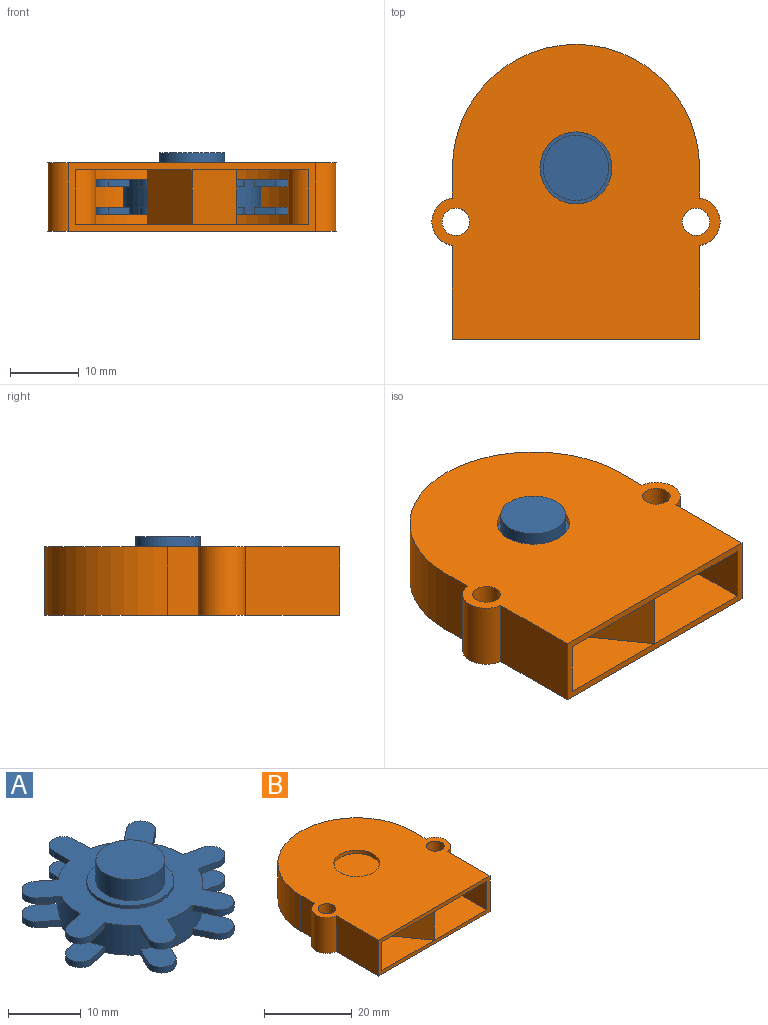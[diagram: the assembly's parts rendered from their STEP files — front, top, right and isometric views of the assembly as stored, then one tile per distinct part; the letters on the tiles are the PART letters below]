
ASSEMBLY  parts=2 mates=1
PART A: 77 faces, bbox 29.3x28.7x11.5 mm
  f0: cylinder r=10mm len=20mm, axis (0,0,1), area 257.8mm2, adj f2,f3,f4,f5,f10,f11,f12,f14
  f1: cylinder r=2mm len=4mm, axis (0,0,1), area 6.3mm2, adj f2,f3,f4,f5
  f2: plane 3.2x1mm, normal (-1,0,0), area 3.2mm2, adj f0,f1,f4,f5
  f3: plane 3.2x1mm, normal (1,0,0), area 3.2mm2, adj f0,f1,f4,f5
  f4: plane 29.35x28.71mm, normal (0,0,-1), area 330.9mm2, adj f0,f1,f2,f3,f6,f9,f11,f12
  f5: plane 5.2x4mm, normal (0,0,1), area 18.6mm2, adj f0,f1,f2,f3
  f6: cylinder r=6mm len=12mm, axis (0,0,1), area 18.8mm2, adj f4,f7
  f7: plane 12x12mm, normal (0,0,-1), area 42.2mm2, adj f6,f8
  f8: cylinder r=4.75mm len=9.5mm, axis (0,0,1), area 59.7mm2, adj f7,f74
  f9: cylinder r=2mm len=3.95mm, axis (0,0,1), area 6.3mm2, adj f4,f10,f11,f12
  f10: plane 5.57x4.66mm, normal (0,0,1), area 18.6mm2, adj f0,f9,f11,f12
  f11: plane 3.12x1mm, normal (0.22,-0.97,0), area 3.2mm2, adj f0,f4,f9,f10
  f12: plane 3.12x1mm, normal (-0.22,0.97,0), area 3.2mm2, adj f0,f4,f9,f10
  f13: cylinder r=2mm len=3.8mm, axis (0,0,1), area 6.3mm2, adj f4,f14,f15,f16
  f14: plane 5.75x5.19mm, normal (0,0,1), area 18.6mm2, adj f0,f13,f15,f16
  f15: plane 2.89x1.39mm, normal (0.9,0.43,0), area 3.2mm2, adj f0,f4,f13,f14
  f16: plane 2.89x1.39mm, normal (-0.9,-0.43,0), area 3.2mm2, adj f0,f4,f13,f14
  f17: cylinder r=2mm len=3.56mm, axis (0,0,1), area 6.3mm2, adj f4,f18,f19,f20
  f18: plane 5.75x5.56mm, normal (0,0,1), area 18.6mm2, adj f0,f17,f19,f20
  f19: plane 2.5x2mm, normal (-0.62,0.78,0), area 3.2mm2, adj f0,f4,f17,f18
  f20: plane 2.5x2mm, normal (0.62,-0.78,0), area 3.2mm2, adj f0,f4,f17,f18
  f21: cylinder r=2mm len=3.95mm, axis (0,0,1), area 6.3mm2, adj f4,f22,f23,f24
  f22: plane 5.57x4.66mm, normal (0,0,1), area 18.6mm2, adj f0,f21,f23,f24
  f23: plane 3.12x1mm, normal (0.22,0.97,0), area 3.2mm2, adj f0,f4,f21,f22
  f24: plane 3.12x1mm, normal (-0.22,-0.97,0), area 3.2mm2, adj f0,f4,f21,f22
  f25: cylinder r=2mm len=3.8mm, axis (0,0,1), area 6.3mm2, adj f4,f26,f27,f28
  f26: plane 5.75x5.19mm, normal (0,0,1), area 18.6mm2, adj f0,f25,f27,f28
  f27: plane 2.89x1.39mm, normal (0.9,-0.43,0), area 3.2mm2, adj f0,f4,f25,f26
  f28: plane 2.89x1.39mm, normal (-0.9,0.43,0), area 3.2mm2, adj f0,f4,f25,f26
  f29: cylinder r=2mm len=3.56mm, axis (0,0,1), area 6.3mm2, adj f4,f30,f31,f32
  f30: plane 2.5x2mm, normal (-0.62,-0.78,0), area 3.2mm2, adj f0,f4,f29,f32
  f31: plane 2.5x2mm, normal (0.62,0.78,0), area 3.2mm2, adj f0,f4,f29,f32
  f32: plane 5.75x5.56mm, normal (0,0,1), area 18.6mm2, adj f0,f29,f30,f31
  f33: cylinder r=2mm len=4mm, axis (0,0,-1), area 6.3mm2, adj f34,f35,f36,f37
  f34: plane 3.2x1mm, normal (-1,0,0), area 3.2mm2, adj f0,f33,f36,f37
  f35: plane 3.2x1mm, normal (1,0,0), area 3.2mm2, adj f0,f33,f36,f37
  f36: plane 29.35x28.71mm, normal (0,0,1), area 330.9mm2, adj f0,f33,f34,f35,f38,f42,f44,f45
  f37: plane 5.2x4mm, normal (0,0,-1), area 18.6mm2, adj f0,f33,f34,f35
  f38: cylinder r=6mm len=12mm, axis (0,0,-1), area 18.8mm2, adj f36,f39
  f39: plane 12x12mm, normal (0,0,1), area 42.2mm2, adj f38,f40
  f40: cylinder r=4.75mm len=9.5mm, axis (0,0,-1), area 104.5mm2, adj f39,f41
  f41: plane 9.5x9.5mm, normal (0,0,1), area 70.9mm2, adj f40
  f42: cylinder r=2mm len=3.95mm, axis (0,0,-1), area 6.3mm2, adj f36,f43,f44,f45
  f43: plane 5.57x4.66mm, normal (0,0,-1), area 18.6mm2, adj f0,f42,f44,f45
  f44: plane 3.12x1mm, normal (0.22,-0.97,0), area 3.2mm2, adj f0,f36,f42,f43
  f45: plane 3.12x1mm, normal (-0.22,0.97,0), area 3.2mm2, adj f0,f36,f42,f43
  f46: cylinder r=2mm len=3.8mm, axis (0,0,-1), area 6.3mm2, adj f36,f47,f48,f49
  f47: plane 5.75x5.19mm, normal (0,0,-1), area 18.6mm2, adj f0,f46,f48,f49
  f48: plane 2.89x1.39mm, normal (0.9,0.43,0), area 3.2mm2, adj f0,f36,f46,f47
  f49: plane 2.89x1.39mm, normal (-0.9,-0.43,0), area 3.2mm2, adj f0,f36,f46,f47
  f50: cylinder r=2mm len=3.56mm, axis (0,0,-1), area 6.3mm2, adj f36,f51,f52,f53
  f51: plane 5.75x5.56mm, normal (0,0,-1), area 18.6mm2, adj f0,f50,f52,f53
  f52: plane 2.5x2mm, normal (-0.62,0.78,0), area 3.2mm2, adj f0,f36,f50,f51
  f53: plane 2.5x2mm, normal (0.62,-0.78,0), area 3.2mm2, adj f0,f36,f50,f51
  f54: cylinder r=2mm len=3.95mm, axis (0,0,-1), area 6.3mm2, adj f36,f55,f56,f57
  f55: plane 5.57x4.66mm, normal (0,0,-1), area 18.6mm2, adj f0,f54,f56,f57
  f56: plane 3.12x1mm, normal (0.22,0.97,0), area 3.2mm2, adj f0,f36,f54,f55
  f57: plane 3.12x1mm, normal (-0.22,-0.97,0), area 3.2mm2, adj f0,f36,f54,f55
  f58: cylinder r=2mm len=3.8mm, axis (0,0,-1), area 6.3mm2, adj f36,f59,f60,f61
  f59: plane 5.75x5.19mm, normal (0,0,-1), area 18.6mm2, adj f0,f58,f60,f61
  f60: plane 2.89x1.39mm, normal (0.9,-0.43,0), area 3.2mm2, adj f0,f36,f58,f59
  f61: plane 2.89x1.39mm, normal (-0.9,0.43,0), area 3.2mm2, adj f0,f36,f58,f59
  f62: cylinder r=2mm len=3.56mm, axis (0,0,-1), area 6.3mm2, adj f36,f63,f64,f65
  f63: plane 2.5x2mm, normal (-0.62,-0.78,0), area 3.2mm2, adj f0,f36,f62,f65
  f64: plane 2.5x2mm, normal (0.62,0.78,0), area 3.2mm2, adj f0,f36,f62,f65
  f65: plane 5.75x5.56mm, normal (0,0,-1), area 18.6mm2, adj f0,f62,f63,f64
  f66: cylinder r=2.95mm len=7.61mm, axis (0,0,-1), area 84.4mm2, adj f67,f68,f70,f71,f72,f73,f75
  f67: cone r=2.2mm half-angle=45deg, axis (0,0,-1), area 6mm2, adj f66,f69,f71,f73
  f68: cone r=2.2mm half-angle=45deg, axis (0,0,-1), area 6mm2, adj f66,f69,f71,f73
  f69: plane 4.11x4mm, normal (0,0,-1), area 13.2mm2, adj f67,f68,f71,f73
  f70: plane 4.34x0.95mm, normal (0,0,-1), area 2.8mm2, adj f66,f71
  f71: plane 6.7x4.34mm, normal (0,1,0), area 27.8mm2, adj f66,f67,f68,f69,f70
  f72: plane 4.34x0.95mm, normal (0,0,-1), area 2.8mm2, adj f66,f73
  f73: plane 6.7x4.34mm, normal (0,-1,0), area 27.8mm2, adj f66,f67,f68,f69,f72
  f74: plane 9.5x9.5mm, normal (0,0,-1), area 5.8mm2, adj f8,f76
  f75: plane 9.1x9.1mm, normal (0,0,-1), area 37.7mm2, adj f66,f76
  f76: cylinder r=4.55mm len=9.1mm, axis (0,0,-1), area 38.6mm2, adj f74,f75
PART B: 26 faces, bbox 42x43x10 mm
  f0: plane 43x42mm, normal (0,0,-1), area 1328.7mm2, adj f1,f2,f5,f8,f9,f10,f16,f18
  f1: plane 10x4.39mm, normal (1,0,0), area 43.9mm2, adj f0,f10,f22,f23
  f2: plane 13.69x10mm, normal (1,0,0), area 136.9mm2, adj f0,f8,f22,f23
  f3: plane 13.69x8mm, normal (-1,0,0), area 109.5mm2, adj f7,f8,f20,f24
  f4: plane 8x4.39mm, normal (-1,0,0), area 35.1mm2, adj f7,f11,f20,f24
  f5: plane 10x4.39mm, normal (-1,0,0), area 43.9mm2, adj f0,f10,f18,f23
  f6: plane 13.69x8mm, normal (1,0,0), area 109.5mm2, adj f7,f8,f17,f24
  f7: plane 42x34mm, normal (0,0,1), area 1136.7mm2, adj f3,f4,f6,f8,f11,f12,f13,f14
  f8: plane 36x10mm, normal (0,-1,0), area 88mm2, adj f0,f2,f3,f6,f7,f9,f23,f24
  f9: plane 13.69x10mm, normal (-1,0,0), area 136.9mm2, adj f0,f8,f18,f23
  f10: cylinder r=18mm len=36mm, axis (0,0,1), area 565.5mm2, adj f0,f1,f5,f23
  f11: cylinder r=17mm len=34mm, axis (0,0,-1), area 427.3mm2, adj f4,f7,f12,f24
  f12: plane 8x4.39mm, normal (1,0,0), area 35.1mm2, adj f7,f11,f17,f24
  f13: plane 9.3x8mm, normal (0.82,-0.57,0), area 90.8mm2, adj f7,f14,f15,f24
  f14: plane 9.3x8mm, normal (-0.82,-0.57,0), area 90.8mm2, adj f7,f13,f15,f24
  f15: cylinder r=17mm len=13.02mm, axis (0,0,-1), area 106.9mm2, adj f7,f13,f14,f24
  f16: cylinder r=5.25mm len=10.5mm, axis (0,0,1), area 33mm2, adj f0,f7
  f17: cylinder r=3.5mm len=8mm, axis (0,0,-1), area 79.9mm2, adj f6,f7,f12,f24
  f18: cylinder r=3.5mm len=10mm, axis (0,0,-1), area 99.9mm2, adj f0,f5,f9,f23
  f19: cylinder r=2mm len=10mm, axis (0,0,-1), area 125.7mm2, adj f0,f23
  f20: cylinder r=3.5mm len=8mm, axis (0,0,-1), area 79.9mm2, adj f3,f4,f7,f24
  f21: cylinder r=2mm len=10mm, axis (0,0,-1), area 125.7mm2, adj f0,f23
  f22: cylinder r=3.5mm len=10mm, axis (0,0,-1), area 99.9mm2, adj f0,f1,f2,f23
  f23: plane 43x42mm, normal (0,0,1), area 1328.7mm2, adj f1,f2,f5,f8,f9,f10,f18,f19
  f24: plane 42x34mm, normal (0,0,-1), area 1136.7mm2, adj f3,f4,f6,f8,f11,f12,f13,f14
  f25: cylinder r=5.25mm len=10.5mm, axis (0,0,-1), area 33mm2, adj f23,f24
PLACE A t=(0,0,12.4)mm
PLACE B t=(0,0,12.4)mm
MATE revolute A.f6 <-> B.f16  axis (0,0,-1) through (0,0,10.9)mm
